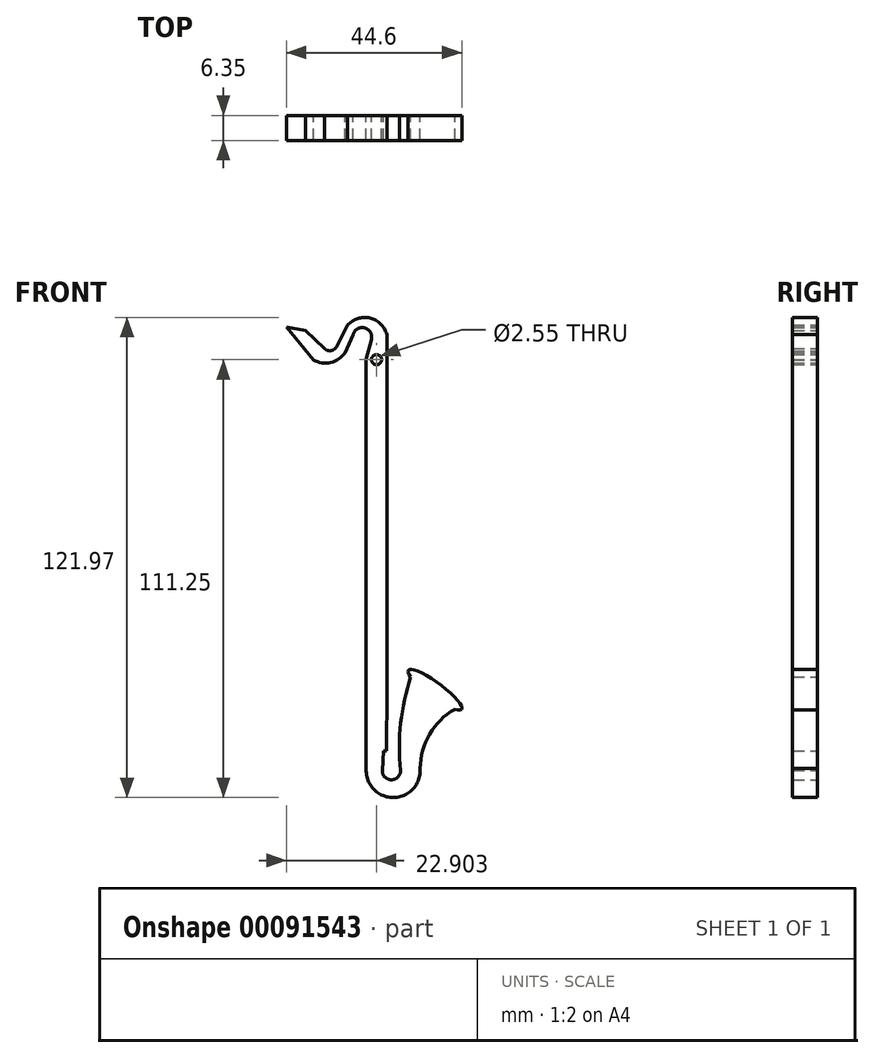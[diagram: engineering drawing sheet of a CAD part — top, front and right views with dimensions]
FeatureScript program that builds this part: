
annotation { "Feature Type Name" : "Feature", "Feature Type Description" : "" }
export const myFeature = defineFeature(function(context is Context, id is Id, definition is map)
    precondition{}
    {
        {
            var Q0;
            Q0=qCreatedBy(makeId("Front.planeOp"),FACE);
            var sketch = newSketch(context, id + "F0", { "sketchPlane" : qUnion([Q0])});
            skEllipse(sketch, "E0", {"center": v(14.66, -30.28) * mm, "majorRadius": 8.38 * mm, "minorRadius": 1.84 * mm, "majorAxis": v(0.8, -0.6)});
            skArc(sketch, "E1", {"start": v(-2.8, -50.52) * mm, "mid": v(4.14, -57.67) * mm, "end": v(10.9, -50.33) * mm});
            skArc(sketch, "E2", {"start": v(19.7, -35.24) * mm, "mid": v(13.27, -41.6) * mm, "end": v(10.9, -50.33) * mm});
            skPoint(sketch, "E2.startSnap0", {"position": v(21.4, -35.24) * mm});
            skLineSegment(sketch, "E3", {"start": v(0, 0) * mm, "end": v(4.05, -50.81) * mm, "construction": true});
            skLineSegment(sketch, "E4", {"start": v(0, 0) * mm, "end": v(16.45, 0) * mm, "construction": true});
            skLineSegment(sketch, "E5", {"start": v(4.05, -50.81) * mm, "end": v(28.33, -50.4) * mm, "construction": true});
            skArc(sketch, "E6", {"start": v(1.27, -50.81) * mm, "mid": v(3.6, -53.17) * mm, "end": v(5.9, -50.78) * mm});
            skLineSegment(sketch, "E7", {"start": v(3.6, -50.85) * mm, "end": v(4.05, -50.81) * mm});
            skArc(sketch, "E8", {"start": v(8.48, -27.04) * mm, "mid": v(5.96, -38.77) * mm, "end": v(5.9, -50.78) * mm});
            skLineSegment(sketch, "E9", {"start": v(63.65, -45.03) * mm, "end": v(28.33, -50.4) * mm, "construction": true});
            skLineSegment(sketch, "E10", {"start": v(-2.8, -50.52) * mm, "end": v(-2.8, 0) * mm});
            skLineSegment(sketch, "E11", {"start": v(-2.8, 0) * mm, "end": v(-2.8, 53.58) * mm});
            skLineSegment(sketch, "E12", {"start": v(1.27, -50.81) * mm, "end": v(1.53, -45.84) * mm});
            skLineSegment(sketch, "E13", {"start": v(1.53, -45.84) * mm, "end": v(2.37, -45.84) * mm});
            skLineSegment(sketch, "E14", {"start": v(2.37, -45.84) * mm, "end": v(2.41, -30.3) * mm});
            skLineSegment(sketch, "E15", {"start": v(2.41, -30.3) * mm, "end": v(2.41, 53.58) * mm});
            skLineSegment(sketch, "E16", {"start": v(-2.8, 53.58) * mm, "end": v(-1.5, 58.73) * mm});
            skArc(sketch, "E17", {"start": v(-1.5, 58.73) * mm, "mid": v(-3.27, 61.66) * mm, "end": v(-6.16, 59.81) * mm});
            skLineSegment(sketch, "E18", {"start": v(2.41, 53.58) * mm, "end": v(2.41, 60.02) * mm});
            skArc(sketch, "E19", {"start": v(2.41, 60.02) * mm, "mid": v(-1.86, 64.15) * mm, "end": v(-7.53, 62.33) * mm});
            skLineSegment(sketch, "E20", {"start": v(-3.18, 58.51) * mm, "end": v(-1.5, 58.73) * mm});
            skLineSegment(sketch, "E21", {"start": v(-6.16, 59.81) * mm, "end": v(-8.15, 55.33) * mm});
            skLineSegment(sketch, "E22", {"start": v(-7.53, 62.33) * mm, "end": v(-10.4, 56.83) * mm});
            skLineSegment(sketch, "E23", {"start": v(-6.16, 59.81) * mm, "end": v(-1.5, 58.73) * mm, "construction": true});
            skLineSegment(sketch, "E24", {"start": v(-7.53, 62.33) * mm, "end": v(-6.16, 59.81) * mm, "construction": true});
            skArc(sketch, "E25", {"start": v(-13.37, 56.38) * mm, "mid": v(-11.77, 55.85) * mm, "end": v(-10.4, 56.83) * mm});
            skArc(sketch, "E26", {"start": v(-16.21, 53.53) * mm, "mid": v(-11.83, 52.87) * mm, "end": v(-8.15, 55.33) * mm});
            skLineSegment(sketch, "E27", {"start": v(-13.17, 58.84) * mm, "end": v(-12.05, 57.7) * mm});
            skLineSegment(sketch, "E28", {"start": v(-16.21, 53.53) * mm, "end": v(-23.1, 61.84) * mm});
            skLineSegment(sketch, "E29", {"start": v(-23.1, 61.84) * mm, "end": v(-18.23, 60.98) * mm});
            skLineSegment(sketch, "E30", {"start": v(-18.23, 60.98) * mm, "end": v(-13.37, 56.38) * mm});
            skLineSegment(sketch, "E31", {"start": v(-16.21, 53.53) * mm, "end": v(-2.8, 53.58) * mm, "construction": true});
            skLineSegment(sketch, "E32", {"start": v(-2.8, 53.58) * mm, "end": v(2.41, 53.58) * mm});
            skCircle(sketch, "E33", {"center": v(-0.2, 53.58) * mm, "radius": 1.27 * mm});
            skSolve(sketch);
        }
        {
            var Q0;
            Q0 = qSketchRegion(id + "F0", true);
            var Q1;
            Q1=sQuery(id+"F0.wireOp",EDGE,"E9");
            var Q2;
            Q2=sQuery(id+"F0.wireOp",EDGE,"E5");
            extrude(context, id + "F1", {"entities" : qUnion([Q0]), "surfaceEntities" : qUnion([Q1, Q2]), "depth" : 6.35 * mm});
        }
    });
